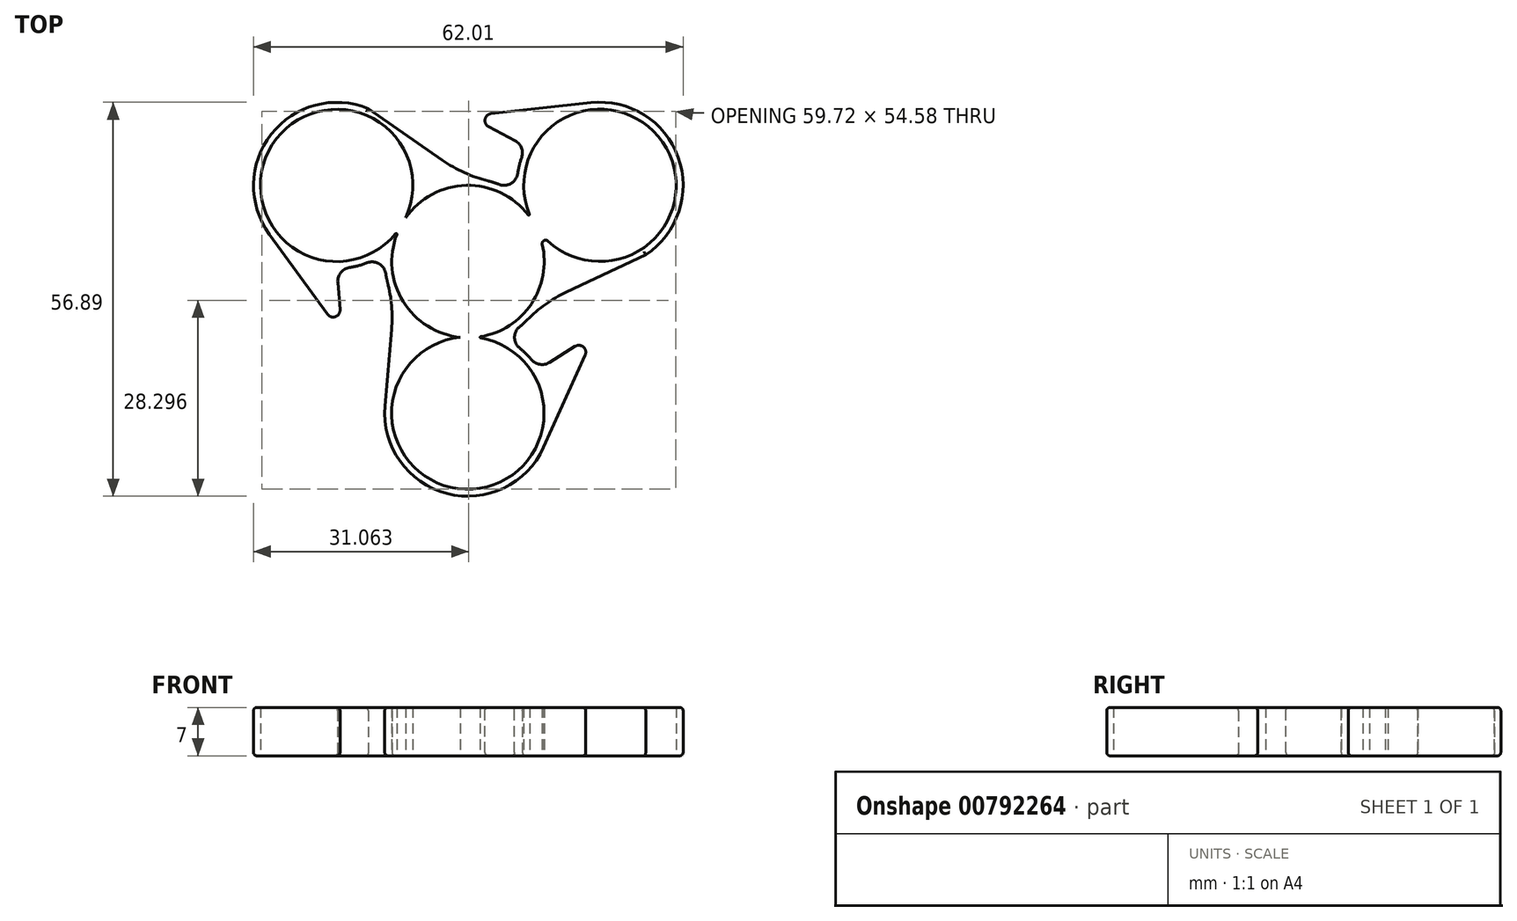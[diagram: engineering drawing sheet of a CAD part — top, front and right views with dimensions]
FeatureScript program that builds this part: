
annotation { "Feature Type Name" : "Feature", "Feature Type Description" : "" }
export const myFeature = defineFeature(function(context is Context, id is Id, definition is map)
    precondition{}
    {
        {
            var Q0;
            Q0=qCreatedBy(makeId("Top.planeOp"),FACE);
            var sketch = newSketch(context, id + "F0", { "sketchPlane" : qUnion([Q0])});
            skCircle(sketch, "E0", {"center": v(-71.75, -0.01) * mm, "radius": 11 * mm});
            skPoint(sketch, "E0.centerSnap0", {"position": v(-71.75, 10.99) * mm});
            skCircle(sketch, "E1", {"center": v(-71.73, 21.88) * mm, "radius": 11 * mm});
            skPoint(sketch, "E2.0.midPoint", {"position": v(-81.26, 16.38) * mm});
            skCircle(sketch, "E3", {"center": v(-52.68, 32.88) * mm, "radius": 11 * mm});
            skPoint(sketch, "E3.centerSnap0", {"position": v(-62.2, 27.38) * mm});
            skLineSegment(sketch, "E4.0", {"start": v(-52.68, 32.88) * mm, "end": v(-62.2, 27.38) * mm, "construction": true});
            skLineSegment(sketch, "E5.0", {"start": v(-71.73, 21.88) * mm, "end": v(-81.26, 16.38) * mm, "construction": true});
            skCircle(sketch, "E6", {"center": v(-90.7, 32.86) * mm, "radius": 11 * mm});
            skPoint(sketch, "E6.centerSnap0", {"position": v(-81.17, 27.36) * mm});
            skLineSegment(sketch, "E7.0", {"start": v(-90.7, 32.86) * mm, "end": v(-81.17, 27.36) * mm, "construction": true});
            skLineSegment(sketch, "E8.0", {"start": v(-71.64, 21.86) * mm, "end": v(-62.11, 16.36) * mm, "construction": true});
            skCircle(sketch, "E9.0", {"center": v(-71.75, -0.01) * mm, "radius": 12 * mm});
            skCircle(sketch, "E10.0", {"center": v(-52.68, 32.88) * mm, "radius": 12 * mm});
            skCircle(sketch, "E11.0", {"center": v(-90.7, 32.86) * mm, "radius": 12 * mm});
            skCircle(sketch, "E12.0", {"center": v(-71.73, 21.88) * mm, "radius": 12 * mm});
            skLineSegment(sketch, "E13", {"start": v(-71.64, 33.88) * mm, "end": v(-86.14, 43.97) * mm});
            skLineSegment(sketch, "E14", {"start": v(-82.4, 16.38) * mm, "end": v(-83.8, 0) * mm});
            skLineSegment(sketch, "E15", {"start": v(-61.52, 15.57) * mm, "end": v(-46.07, 22.86) * mm});
            skLineSegment(sketch, "E16", {"start": v(-89.92, 11.38) * mm, "end": v(-100.4, 25.81) * mm});
            skLineSegment(sketch, "E17", {"start": v(-53.45, 11.36) * mm, "end": v(-60.82, -4.95) * mm});
            skPoint(sketch, "E18", {"position": v(-71.64, 32.88) * mm});
            skLineSegment(sketch, "E19", {"start": v(-71.64, 42.88) * mm, "end": v(-53.98, 44.8) * mm});
            skLineSegment(sketch, "E20", {"start": v(-89.92, 11.38) * mm, "end": v(-90.7, 20.86) * mm});
            skPoint(sketch, "E21", {"position": v(-63.3, 38.48) * mm});
            skLineSegment(sketch, "E22", {"start": v(-71.64, 42.88) * mm, "end": v(-63.3, 38.48) * mm});
            skPoint(sketch, "E23", {"position": v(-61.56, 6.32) * mm});
            skLineSegment(sketch, "E24", {"start": v(-53.45, 11.36) * mm, "end": v(-61.56, 6.32) * mm});
            skSolve(sketch);
        }
        {
            var Q0;
            {var subQ0=sQuery(id+"F0.wireOp",EDGE,"E12.0");var subQ1=sQuery(id+"F0.wireOp",EDGE,"E6");var subQ9=makeQuery(id+"F0.imprint","INTERSECT",VERTEX,{"disambiguationData":[OD(0.0)],"derivedFrom":[subQ1,subQ0]});Q0=makeQuery(id+"F0.imprint","IMPRINT",FACE,{"disambiguationData":[TD([[makeQuery(id+"F0.imprint","IMPRINT",EDGE,{"disambiguationData":[TD([[subQ9,1.0]])],"derivedFrom":subQ1}),-1.0]])]});}
            var Q1;
            {var subQ0=sQuery(id+"F0.wireOp",EDGE,"E12.0");var subQ1=sQuery(id+"F0.wireOp",EDGE,"E3");var subQ9=makeQuery(id+"F0.imprint","INTERSECT",VERTEX,{"disambiguationData":[OD(0.0)],"derivedFrom":[subQ1,subQ0]});Q1=makeQuery(id+"F0.imprint","IMPRINT",FACE,{"disambiguationData":[TD([[makeQuery(id+"F0.imprint","IMPRINT",EDGE,{"disambiguationData":[TD([[subQ9,1.0]])],"derivedFrom":subQ1}),-1.0]])]});}
            var Q2;
            {var subQ0=sQuery(id+"F0.wireOp",EDGE,"E13");var subQ1=sQuery(id+"F0.wireOp",EDGE,"E11.0");var subQ2=makeQuery(id+"F0.imprint","INTERSECT",VERTEX,{"disambiguationData":[OD(1.0)],"derivedFrom":[subQ1,subQ0]});Q2=makeQuery(id+"F0.imprint","IMPRINT",FACE,{"disambiguationData":[TD([[makeQuery(id+"F0.imprint","IMPRINT",EDGE,{"disambiguationData":[TD([[subQ2,1.0]])],"derivedFrom":subQ1}),-1.0]])]});}
            var Q3;
            {var subQ0=sQuery(id+"F0.wireOp",EDGE,"E15");var subQ1=sQuery(id+"F0.wireOp",EDGE,"E10.0");var subQ2=makeQuery(id+"F0.imprint","INTERSECT",VERTEX,{"disambiguationData":[OD(1.0)],"derivedFrom":[subQ1,subQ0]});Q3=makeQuery(id+"F0.imprint","IMPRINT",FACE,{"disambiguationData":[TD([[makeQuery(id+"F0.imprint","IMPRINT",EDGE,{"disambiguationData":[TD([[subQ2,1.0]])],"derivedFrom":subQ1}),-1.0]])]});}
            var Q4;
            {var subQ0=sQuery(id+"F0.wireOp",EDGE,"E14");var subQ1=sQuery(id+"F0.wireOp",EDGE,"E9.0");var subQ2=makeQuery(id+"F0.imprint","INTERSECT",VERTEX,{"derivedFrom":[subQ1,subQ0]});Q4=makeQuery(id+"F0.imprint","IMPRINT",FACE,{"disambiguationData":[TD([[makeQuery(id+"F0.imprint","IMPRINT",EDGE,{"disambiguationData":[TD([[subQ2,1.0]])],"derivedFrom":subQ1}),-1.0]])]});}
            var Q5;
            {var subQ0=sQuery(id+"F0.wireOp",EDGE,"E12.0");var subQ1=sQuery(id+"F0.wireOp",EDGE,"E0");var subQ7=makeQuery(id+"F0.imprint","INTERSECT",VERTEX,{"disambiguationData":[OD(0.0)],"derivedFrom":[subQ1,subQ0]});Q5=makeQuery(id+"F0.imprint","IMPRINT",FACE,{"disambiguationData":[TD([[makeQuery(id+"F0.imprint","IMPRINT",EDGE,{"disambiguationData":[TD([[subQ7,1.0]])],"derivedFrom":subQ1}),-1.0]])]});}
            var Q6;
            {var subQ1=sQuery(id+"F0.wireOp",EDGE,"E1");var subQ6=sQuery(id+"F0.wireOp",EDGE,"E9.0");var subQ8=makeQuery(id+"F0.imprint","INTERSECT",VERTEX,{"disambiguationData":[OD(1.0)],"derivedFrom":[subQ1,subQ6]});Q6=makeQuery(id+"F0.imprint","IMPRINT",FACE,{"disambiguationData":[TD([[makeQuery(id+"F0.imprint","IMPRINT",EDGE,{"disambiguationData":[TD([[subQ8,-1.0]])],"derivedFrom":subQ1}),-1.0]])]});}
            var Q7;
            {var subQ1=sQuery(id+"F0.wireOp",EDGE,"E11.0");var subQ3=sQuery(id+"F0.wireOp",EDGE,"E1");var subQ4=makeQuery(id+"F0.imprint","INTERSECT",VERTEX,{"disambiguationData":[OD(1.0)],"derivedFrom":[subQ3,subQ1]});Q7=makeQuery(id+"F0.imprint","IMPRINT",FACE,{"disambiguationData":[TD([[makeQuery(id+"F0.imprint","IMPRINT",EDGE,{"disambiguationData":[TD([[subQ4,-1.0]])],"derivedFrom":subQ3}),-1.0]])]});}
            var Q8;
            {var subQ0=sQuery(id+"F0.wireOp",EDGE,"E11.0");var subQ1=sQuery(id+"F0.wireOp",EDGE,"E1");var subQ2=makeQuery(id+"F0.imprint","INTERSECT",VERTEX,{"disambiguationData":[OD(0.0)],"derivedFrom":[subQ1,subQ0]});Q8=makeQuery(id+"F0.imprint","IMPRINT",FACE,{"disambiguationData":[TD([[makeQuery(id+"F0.imprint","IMPRINT",EDGE,{"disambiguationData":[TD([[subQ2,1.0]])],"derivedFrom":subQ1}),-1.0]])]});}
            var Q9;
            {var subQ0=sQuery(id+"F0.wireOp",EDGE,"E3");var subQ1=sQuery(id+"F0.wireOp",EDGE,"E1");var subQ2=makeQuery(id+"F0.imprint","INTERSECT",VERTEX,{"derivedFrom":[subQ1,subQ0]});Q9=makeQuery(id+"F0.imprint","IMPRINT",FACE,{"disambiguationData":[TD([[makeQuery(id+"F0.imprint","IMPRINT",EDGE,{"disambiguationData":[TD([[subQ2,-1.0]])],"derivedFrom":subQ1}),-1.0]])]});}
            var Q10;
            {var subQ0=sQuery(id+"F0.wireOp",EDGE,"E6");var subQ1=sQuery(id+"F0.wireOp",EDGE,"E1");var subQ2=makeQuery(id+"F0.imprint","INTERSECT",VERTEX,{"disambiguationData":[OD(1.0)],"derivedFrom":[subQ1,subQ0]});Q10=makeQuery(id+"F0.imprint","IMPRINT",FACE,{"disambiguationData":[TD([[makeQuery(id+"F0.imprint","IMPRINT",EDGE,{"disambiguationData":[TD([[subQ2,-1.0]])],"derivedFrom":subQ1}),-1.0]])]});}
            var Q11;
            {var subQ0=sQuery(id+"F0.wireOp",EDGE,"E1");var subQ1=sQuery(id+"F0.wireOp",EDGE,"E0");var subQ2=makeQuery(id+"F0.imprint","INTERSECT",VERTEX,{"disambiguationData":[OD(0.0)],"derivedFrom":[subQ1,subQ0]});Q11=makeQuery(id+"F0.imprint","IMPRINT",FACE,{"disambiguationData":[TD([[makeQuery(id+"F0.imprint","IMPRINT",EDGE,{"disambiguationData":[TD([[subQ2,1.0]])],"derivedFrom":subQ1}),-1.0]])]});}
            var Q12;
            {var subQ0=sQuery(id+"F0.wireOp",EDGE,"E16");Q12=makeQuery(id+"F0.imprint","IMPRINT",FACE,{"disambiguationData":[TD([[makeQuery(id+"F0.imprint","IMPRINT",EDGE,{"derivedFrom":subQ0}),-1.0]])]});}
            var Q13;
            {var subQ0=sQuery(id+"F0.wireOp",EDGE,"E17");Q13=makeQuery(id+"F0.imprint","IMPRINT",FACE,{"disambiguationData":[TD([[makeQuery(id+"F0.imprint","IMPRINT",EDGE,{"derivedFrom":subQ0}),-1.0]])]});}
            var Q14;
            {var subQ0=sQuery(id+"F0.wireOp",EDGE,"E19");Q14=makeQuery(id+"F0.imprint","IMPRINT",FACE,{"disambiguationData":[TD([[makeQuery(id+"F0.imprint","IMPRINT",EDGE,{"derivedFrom":subQ0}),-1.0]])]});}
            extrude(context, id + "F1", {"entities" : qUnion([Q0, Q1, Q2, Q3, Q4, Q5, Q6, Q7, Q8, Q9, Q10, Q11, Q12, Q13, Q14]), "depth" : 7 * mm, "offsetDistance" : 25 * mm});
        }
        {
            var Q0;
            {var subQ0=sQuery(id+"F0.wireOp",EDGE,"E12.0");var subQ1=sQuery(id+"F0.wireOp",EDGE,"E9.0");Q0=makeQuery(id+"F1.opExtrude","SWEPT_EDGE",EDGE,{"disambiguationData":[OSD([subQ1,subQ0]),TDD([makeQuery(id+"F0.imprint","INTERSECT",VERTEX,{"disambiguationData":[OD(0.0)],"derivedFrom":[subQ1,subQ0]})])]});}
            var Q1;
            {var subQ0=sQuery(id+"F0.wireOp",EDGE,"E12.0");var subQ1=sQuery(id+"F0.wireOp",EDGE,"E10.0");Q1=makeQuery(id+"F1.opExtrude","SWEPT_EDGE",EDGE,{"disambiguationData":[OSD([subQ1,subQ0]),TDD([makeQuery(id+"F0.imprint","INTERSECT",VERTEX,{"disambiguationData":[OD(0.0)],"derivedFrom":[subQ1,subQ0]})])]});}
            var Q2;
            {var subQ0=sQuery(id+"F0.wireOp",EDGE,"E12.0");var subQ1=sQuery(id+"F0.wireOp",EDGE,"E11.0");Q2=makeQuery(id+"F1.opExtrude","SWEPT_EDGE",EDGE,{"disambiguationData":[OSD([subQ1,subQ0]),TDD([makeQuery(id+"F0.imprint","INTERSECT",VERTEX,{"disambiguationData":[OD(0.0)],"derivedFrom":[subQ1,subQ0]})])]});}
            fillet(context, id + "F2", {"entities" : qUnion([Q0, Q1, Q2]), "radius" : 2 * mm, "tangentPropagation" : true, "allowEdgeOverflow" : false});
        }
        {
            var Q0;
            Q0=makeQuery(id+"F1.opExtrude","SWEPT_EDGE",EDGE,{"disambiguationData":[OSD([sQuery(id+"F0.wireOp",EDGE,"E1"),sQuery(id+"F0.wireOp",EDGE,"E3")])]});
            var Q1;
            Q1=makeQuery(id+"F1.opExtrude","SWEPT_EDGE",EDGE,{"disambiguationData":[OSD([sQuery(id+"F0.wireOp",EDGE,"E1"),sQuery(id+"F0.wireOp",EDGE,"E6")])]});
            var Q2;
            Q2=makeQuery(id+"F1.opExtrude","SWEPT_EDGE",EDGE,{"disambiguationData":[OSD([sQuery(id+"F0.wireOp",EDGE,"E0"),sQuery(id+"F0.wireOp",EDGE,"E1")])]});
            fillet(context, id + "F3", {"entities" : qUnion([Q0, Q1, Q2]), "radius" : .1 * mm, "tangentPropagation" : true, "allowEdgeOverflow" : false});
        }
        {
            var Q0;
            {var subQ0=sQuery(id+"F0.wireOp",EDGE,"E6");var subQ1=sQuery(id+"F0.wireOp",EDGE,"E1");var subQ2=makeQuery(id+"F0.imprint","INTERSECT",VERTEX,{"disambiguationData":[OD(0.0)],"derivedFrom":[subQ1,subQ0]});Q0=makeQuery(id+"F0.imprint","IMPRINT",FACE,{"disambiguationData":[TD([[makeQuery(id+"F0.imprint","IMPRINT",EDGE,{"disambiguationData":[TD([[subQ2,1.0]])],"derivedFrom":subQ1}),-1.0]])]});}
            var Q1;
            {var subQ0=sQuery(id+"F0.wireOp",EDGE,"E10.0");var subQ1=sQuery(id+"F0.wireOp",EDGE,"E1");var subQ2=makeQuery(id+"F0.imprint","INTERSECT",VERTEX,{"disambiguationData":[OD(0.0)],"derivedFrom":[subQ1,subQ0]});Q1=makeQuery(id+"F0.imprint","IMPRINT",FACE,{"disambiguationData":[TD([[makeQuery(id+"F0.imprint","IMPRINT",EDGE,{"disambiguationData":[TD([[subQ2,-1.0]])],"derivedFrom":subQ1}),-1.0]])]});}
            var Q2;
            {var subQ0=sQuery(id+"F0.wireOp",EDGE,"E1");var subQ1=sQuery(id+"F0.wireOp",EDGE,"E0");var subQ2=makeQuery(id+"F0.imprint","INTERSECT",VERTEX,{"disambiguationData":[OD(1.0)],"derivedFrom":[subQ1,subQ0]});Q2=makeQuery(id+"F0.imprint","IMPRINT",FACE,{"disambiguationData":[TD([[makeQuery(id+"F0.imprint","IMPRINT",EDGE,{"disambiguationData":[TD([[subQ2,-1.0]])],"derivedFrom":subQ1}),-1.0]])]});}
            extrude(context, id + "F4", {"entities" : qUnion([Q0, Q1, Q2]), "operationType" : NewBodyOperationType.ADD, "depth" : 7 * mm, "offsetDistance" : 25 * mm});
        }
        {
            var Q0;
            Q0=makeQuery(id+"F4.opExtrude","SWEPT_EDGE",EDGE,{"disambiguationData":[OSD([sQuery(id+"F0.wireOp",EDGE,"E1"),sQuery(id+"F0.wireOp",EDGE,"E3")])]});
            var Q1;
            {var subQ0=sQuery(id+"F0.wireOp",EDGE,"E1");var subQ2=sQuery(id+"F0.wireOp",EDGE,"E3");Q1=makeQuery(id+"F3.opFillet","BLEND_EDGE",EDGE,{"blendedFrom":[makeQuery(id+"F1.opExtrude","SWEPT_EDGE",EDGE,{"disambiguationData":[OSD([subQ0,subQ2])]}),makeQuery(id+"F1.opExtrude","SWEPT_FACE",FACE,{"disambiguationData":[OSD([subQ0]),TDD([makeQuery(id+"F0.imprint","IMPRINT",EDGE,{"disambiguationData":[TD([[makeQuery(id+"F0.imprint","INTERSECT",VERTEX,{"derivedFrom":[subQ0,subQ2]}),-1.0]])],"derivedFrom":subQ0}),makeQuery(id+"F0.imprint","IMPRINT",EDGE,{"disambiguationData":[TD([[makeQuery(id+"F0.imprint","INTERSECT",VERTEX,{"disambiguationData":[OD(0.0)],"derivedFrom":[subQ0,sQuery(id+"F0.wireOp",EDGE,"E11.0")]}),1.0]])],"derivedFrom":subQ0})])]})],"blendedInto":[makeQuery(id+"F1.opExtrude","SWEPT_FACE",FACE,{"disambiguationData":[OSD([subQ0]),TDD([makeQuery(id+"F0.imprint","IMPRINT",EDGE,{"disambiguationData":[TD([[makeQuery(id+"F0.imprint","INTERSECT",VERTEX,{"derivedFrom":[subQ0,subQ2]}),-1.0]])],"derivedFrom":subQ0}),makeQuery(id+"F0.imprint","IMPRINT",EDGE,{"disambiguationData":[TD([[makeQuery(id+"F0.imprint","INTERSECT",VERTEX,{"disambiguationData":[OD(0.0)],"derivedFrom":[subQ0,sQuery(id+"F0.wireOp",EDGE,"E11.0")]}),1.0]])],"derivedFrom":subQ0})])]})]});}
            fillet(context, id + "F5", {"entities" : qUnion([Q0, Q1]), "radius" : .5 * mm, "tangentPropagation" : true, "allowEdgeOverflow" : false});
        }
        {
            var Q0;
            Q0=makeQuery(id+"F1.opExtrude","SWEPT_EDGE",EDGE,{"disambiguationData":[OSD([sQuery(id+"F0.wireOp",EDGE,"E11.0"),sQuery(id+"F0.wireOp",EDGE,"E20")])]});
            var Q1;
            Q1=makeQuery(id+"F1.opExtrude","SWEPT_EDGE",EDGE,{"disambiguationData":[OSD([sQuery(id+"F0.wireOp",EDGE,"E10.0"),sQuery(id+"F0.wireOp",EDGE,"E22")])]});
            var Q2;
            Q2=makeQuery(id+"F1.opExtrude","SWEPT_EDGE",EDGE,{"disambiguationData":[OSD([sQuery(id+"F0.wireOp",EDGE,"E9.0"),sQuery(id+"F0.wireOp",EDGE,"E24")])]});
            fillet(context, id + "F6", {"entities" : qUnion([Q0, Q1, Q2]), "radius" : 2 * mm, "tangentPropagation" : true, "allowEdgeOverflow" : false});
        }
        {
            var Q0;
            Q0=makeQuery(id+"F1.opExtrude","SWEPT_EDGE",EDGE,{"disambiguationData":[OSD([sQuery(id+"F0.wireOp",EDGE,"E17"),sQuery(id+"F0.wireOp",EDGE,"E24")])]});
            var Q1;
            Q1=makeQuery(id+"F1.opExtrude","SWEPT_EDGE",EDGE,{"disambiguationData":[OSD([sQuery(id+"F0.wireOp",EDGE,"E19"),sQuery(id+"F0.wireOp",EDGE,"E22")])]});
            var Q2;
            Q2=makeQuery(id+"F1.opExtrude","SWEPT_EDGE",EDGE,{"disambiguationData":[OSD([sQuery(id+"F0.wireOp",EDGE,"E16"),sQuery(id+"F0.wireOp",EDGE,"E20")])]});
            fillet(context, id + "F7", {"entities" : qUnion([Q0, Q1, Q2]), "radius" : 1 * mm, "tangentPropagation" : true, "allowEdgeOverflow" : false});
        }
        {
            var Q0;
            Q0=makeQuery(id+"F1.opExtrude","SWEPT_EDGE",EDGE,{"disambiguationData":[OSD([sQuery(id+"F0.wireOp",EDGE,"E12.0"),sQuery(id+"F0.wireOp",EDGE,"E14")])]});
            var Q1;
            Q1=makeQuery(id+"F1.opExtrude","SWEPT_EDGE",EDGE,{"disambiguationData":[OSD([sQuery(id+"F0.wireOp",EDGE,"E12.0"),sQuery(id+"F0.wireOp",EDGE,"E15")])]});
            var Q2;
            Q2=makeQuery(id+"F1.opExtrude","SWEPT_EDGE",EDGE,{"disambiguationData":[OSD([sQuery(id+"F0.wireOp",EDGE,"E12.0"),sQuery(id+"F0.wireOp",EDGE,"E13")])]});
            fillet(context, id + "F8", {"entities" : qUnion([Q0, Q1, Q2]), "radius" : 20 * mm, "tangentPropagation" : true, "allowEdgeOverflow" : false});
        }
        {
            var Q0;
            {var subQ0=sQuery(id+"F0.wireOp",EDGE,"E9.0");Q0=makeQuery(id+"F1.opExtrude","CAP_EDGE",EDGE,{"disambiguationData":[OSD([subQ0]),TDD([makeQuery(id+"F0.imprint","IMPRINT",EDGE,{"disambiguationData":[TD([[makeQuery(id+"F0.imprint","INTERSECT",VERTEX,{"derivedFrom":[subQ0,sQuery(id+"F0.wireOp",EDGE,"E17")]}),1.0]])],"derivedFrom":subQ0})])],"isStart":false});}
            var Q1;
            Q1=makeQuery(id+"F1.opExtrude","CAP_EDGE",EDGE,{"disambiguationData":[OSD([sQuery(id+"F0.wireOp",EDGE,"E17")])],"isStart":false});
            var Q2;
            {var subQ0=sQuery(id+"F0.wireOp",EDGE,"E12.0");var subQ1=sQuery(id+"F0.wireOp",EDGE,"E10.0");var subQ2=sQuery(id+"F0.wireOp",EDGE,"E3");var subQ3=sQuery(id+"F0.wireOp",EDGE,"E1");var subQ4=sQuery(id+"F0.wireOp",EDGE,"E11.0");var subQ5=sQuery(id+"F0.wireOp",EDGE,"E6");var subQ6=sQuery(id+"F0.wireOp",EDGE,"E9.0");var subQ7=sQuery(id+"F0.wireOp",EDGE,"E0");var subQ8=sQuery(id+"F0.wireOp",EDGE,"E15");Q2=makeQuery(id+"F8.opFillet","BLEND_EDGE",EDGE,{"blendedFrom":[makeQuery(id+"F1.opExtrude","SWEPT_EDGE",EDGE,{"disambiguationData":[OSD([subQ0,subQ8])]}),makeQuery(id+"F4.boolean.opBoolean","MERGE",FACE,{"derivedFrom":[makeQuery(id+"F1.opExtrude","CAP_FACE",FACE,{"disambiguationData":[OSD([subQ7,subQ3,subQ2,subQ5,subQ6,subQ1,subQ4,subQ0,sQuery(id+"F0.wireOp",EDGE,"E13"),sQuery(id+"F0.wireOp",EDGE,"E14"),subQ8,sQuery(id+"F0.wireOp",EDGE,"E16"),sQuery(id+"F0.wireOp",EDGE,"E17"),sQuery(id+"F0.wireOp",EDGE,"E19"),sQuery(id+"F0.wireOp",EDGE,"E20"),sQuery(id+"F0.wireOp",EDGE,"E22"),sQuery(id+"F0.wireOp",EDGE,"E24")])],"isStart":false}),makeQuery(id+"F4.opExtrude","CAP_FACE",FACE,{"disambiguationData":[OSD([subQ7,subQ3,subQ6,subQ0])],"isStart":false}),makeQuery(id+"F4.opExtrude","CAP_FACE",FACE,{"disambiguationData":[OSD([subQ3,subQ5,subQ4,subQ0])],"isStart":false}),makeQuery(id+"F4.opExtrude","CAP_FACE",FACE,{"disambiguationData":[OSD([subQ3,subQ2,subQ1,subQ0])],"isStart":false})]})],"blendedInto":[makeQuery(id+"F4.boolean.opBoolean","MERGE",FACE,{"derivedFrom":[makeQuery(id+"F1.opExtrude","CAP_FACE",FACE,{"disambiguationData":[OSD([subQ7,subQ3,subQ2,subQ5,subQ6,subQ1,subQ4,subQ0,sQuery(id+"F0.wireOp",EDGE,"E13"),sQuery(id+"F0.wireOp",EDGE,"E14"),subQ8,sQuery(id+"F0.wireOp",EDGE,"E16"),sQuery(id+"F0.wireOp",EDGE,"E17"),sQuery(id+"F0.wireOp",EDGE,"E19"),sQuery(id+"F0.wireOp",EDGE,"E20"),sQuery(id+"F0.wireOp",EDGE,"E22"),sQuery(id+"F0.wireOp",EDGE,"E24")])],"isStart":false}),makeQuery(id+"F4.opExtrude","CAP_FACE",FACE,{"disambiguationData":[OSD([subQ7,subQ3,subQ6,subQ0])],"isStart":false}),makeQuery(id+"F4.opExtrude","CAP_FACE",FACE,{"disambiguationData":[OSD([subQ3,subQ5,subQ4,subQ0])],"isStart":false}),makeQuery(id+"F4.opExtrude","CAP_FACE",FACE,{"disambiguationData":[OSD([subQ3,subQ2,subQ1,subQ0])],"isStart":false})]})]});}
            var Q3;
            {var subQ0=sQuery(id+"F0.wireOp",EDGE,"E12.0");Q3=makeQuery(id+"F1.opExtrude","CAP_EDGE",EDGE,{"disambiguationData":[OSD([subQ0]),TDD([makeQuery(id+"F0.imprint","IMPRINT",EDGE,{"disambiguationData":[TD([[makeQuery(id+"F0.imprint","INTERSECT",VERTEX,{"derivedFrom":[subQ0,sQuery(id+"F0.wireOp",EDGE,"E15")]}),1.0]])],"derivedFrom":subQ0})])],"isStart":false});}
            var Q4;
            {var subQ0=sQuery(id+"F0.wireOp",EDGE,"E12.0");var subQ1=sQuery(id+"F0.wireOp",EDGE,"E9.0");Q4=makeQuery(id+"F2.opFillet","BLEND_EDGE",EDGE,{"blendedFrom":[makeQuery(id+"F1.opExtrude","SWEPT_EDGE",EDGE,{"disambiguationData":[OSD([subQ1,subQ0]),TDD([makeQuery(id+"F0.imprint","INTERSECT",VERTEX,{"disambiguationData":[OD(0.0)],"derivedFrom":[subQ1,subQ0]})])]}),makeQuery(id+"F1.opExtrude","CAP_FACE",FACE,{"disambiguationData":[OSD([sQuery(id+"F0.wireOp",EDGE,"E0"),sQuery(id+"F0.wireOp",EDGE,"E1"),sQuery(id+"F0.wireOp",EDGE,"E3"),sQuery(id+"F0.wireOp",EDGE,"E6"),subQ1,sQuery(id+"F0.wireOp",EDGE,"E10.0"),sQuery(id+"F0.wireOp",EDGE,"E11.0"),subQ0,sQuery(id+"F0.wireOp",EDGE,"E13"),sQuery(id+"F0.wireOp",EDGE,"E14"),sQuery(id+"F0.wireOp",EDGE,"E15"),sQuery(id+"F0.wireOp",EDGE,"E16"),sQuery(id+"F0.wireOp",EDGE,"E17"),sQuery(id+"F0.wireOp",EDGE,"E19"),sQuery(id+"F0.wireOp",EDGE,"E20"),sQuery(id+"F0.wireOp",EDGE,"E22"),sQuery(id+"F0.wireOp",EDGE,"E24")])],"isStart":false})],"blendedInto":[makeQuery(id+"F1.opExtrude","CAP_FACE",FACE,{"disambiguationData":[OSD([sQuery(id+"F0.wireOp",EDGE,"E0"),sQuery(id+"F0.wireOp",EDGE,"E1"),sQuery(id+"F0.wireOp",EDGE,"E3"),sQuery(id+"F0.wireOp",EDGE,"E6"),subQ1,sQuery(id+"F0.wireOp",EDGE,"E10.0"),sQuery(id+"F0.wireOp",EDGE,"E11.0"),subQ0,sQuery(id+"F0.wireOp",EDGE,"E13"),sQuery(id+"F0.wireOp",EDGE,"E14"),sQuery(id+"F0.wireOp",EDGE,"E15"),sQuery(id+"F0.wireOp",EDGE,"E16"),sQuery(id+"F0.wireOp",EDGE,"E17"),sQuery(id+"F0.wireOp",EDGE,"E19"),sQuery(id+"F0.wireOp",EDGE,"E20"),sQuery(id+"F0.wireOp",EDGE,"E22"),sQuery(id+"F0.wireOp",EDGE,"E24")])],"isStart":false})]});}
            var Q5;
            {var subQ0=sQuery(id+"F0.wireOp",EDGE,"E9.0");Q5=makeQuery(id+"F1.opExtrude","CAP_EDGE",EDGE,{"disambiguationData":[OSD([subQ0]),TDD([makeQuery(id+"F0.imprint","IMPRINT",EDGE,{"disambiguationData":[TD([[makeQuery(id+"F0.imprint","INTERSECT",VERTEX,{"derivedFrom":[subQ0,sQuery(id+"F0.wireOp",EDGE,"E24")]}),-1.0]])],"derivedFrom":subQ0})])],"isStart":false});}
            var Q6;
            Q6=makeQuery(id+"F1.opExtrude","CAP_EDGE",EDGE,{"disambiguationData":[OSD([sQuery(id+"F0.wireOp",EDGE,"E24")])],"isStart":false});
            var Q7;
            {var subQ0=sQuery(id+"F0.wireOp",EDGE,"E12.0");var subQ1=sQuery(id+"F0.wireOp",EDGE,"E10.0");var subQ2=sQuery(id+"F0.wireOp",EDGE,"E3");var subQ3=sQuery(id+"F0.wireOp",EDGE,"E1");var subQ4=sQuery(id+"F0.wireOp",EDGE,"E11.0");var subQ5=sQuery(id+"F0.wireOp",EDGE,"E6");var subQ6=sQuery(id+"F0.wireOp",EDGE,"E9.0");var subQ7=sQuery(id+"F0.wireOp",EDGE,"E0");var subQ8=sQuery(id+"F0.wireOp",EDGE,"E24");Q7=makeQuery(id+"F6.opFillet","BLEND_EDGE",EDGE,{"blendedFrom":[makeQuery(id+"F1.opExtrude","SWEPT_EDGE",EDGE,{"disambiguationData":[OSD([subQ6,subQ8])]}),makeQuery(id+"F4.boolean.opBoolean","MERGE",FACE,{"derivedFrom":[makeQuery(id+"F1.opExtrude","CAP_FACE",FACE,{"disambiguationData":[OSD([subQ7,subQ3,subQ2,subQ5,subQ6,subQ1,subQ4,subQ0,sQuery(id+"F0.wireOp",EDGE,"E13"),sQuery(id+"F0.wireOp",EDGE,"E14"),sQuery(id+"F0.wireOp",EDGE,"E15"),sQuery(id+"F0.wireOp",EDGE,"E16"),sQuery(id+"F0.wireOp",EDGE,"E17"),sQuery(id+"F0.wireOp",EDGE,"E19"),sQuery(id+"F0.wireOp",EDGE,"E20"),sQuery(id+"F0.wireOp",EDGE,"E22"),subQ8])],"isStart":false}),makeQuery(id+"F4.opExtrude","CAP_FACE",FACE,{"disambiguationData":[OSD([subQ7,subQ3,subQ6,subQ0])],"isStart":false}),makeQuery(id+"F4.opExtrude","CAP_FACE",FACE,{"disambiguationData":[OSD([subQ3,subQ5,subQ4,subQ0])],"isStart":false}),makeQuery(id+"F4.opExtrude","CAP_FACE",FACE,{"disambiguationData":[OSD([subQ3,subQ2,subQ1,subQ0])],"isStart":false})]})],"blendedInto":[makeQuery(id+"F4.boolean.opBoolean","MERGE",FACE,{"derivedFrom":[makeQuery(id+"F1.opExtrude","CAP_FACE",FACE,{"disambiguationData":[OSD([subQ7,subQ3,subQ2,subQ5,subQ6,subQ1,subQ4,subQ0,sQuery(id+"F0.wireOp",EDGE,"E13"),sQuery(id+"F0.wireOp",EDGE,"E14"),sQuery(id+"F0.wireOp",EDGE,"E15"),sQuery(id+"F0.wireOp",EDGE,"E16"),sQuery(id+"F0.wireOp",EDGE,"E17"),sQuery(id+"F0.wireOp",EDGE,"E19"),sQuery(id+"F0.wireOp",EDGE,"E20"),sQuery(id+"F0.wireOp",EDGE,"E22"),subQ8])],"isStart":false}),makeQuery(id+"F4.opExtrude","CAP_FACE",FACE,{"disambiguationData":[OSD([subQ7,subQ3,subQ6,subQ0])],"isStart":false}),makeQuery(id+"F4.opExtrude","CAP_FACE",FACE,{"disambiguationData":[OSD([subQ3,subQ5,subQ4,subQ0])],"isStart":false}),makeQuery(id+"F4.opExtrude","CAP_FACE",FACE,{"disambiguationData":[OSD([subQ3,subQ2,subQ1,subQ0])],"isStart":false})]})]});}
            var Q8;
            {var subQ0=sQuery(id+"F0.wireOp",EDGE,"E12.0");var subQ1=sQuery(id+"F0.wireOp",EDGE,"E10.0");var subQ2=sQuery(id+"F0.wireOp",EDGE,"E3");var subQ3=sQuery(id+"F0.wireOp",EDGE,"E1");var subQ4=sQuery(id+"F0.wireOp",EDGE,"E11.0");var subQ5=sQuery(id+"F0.wireOp",EDGE,"E6");var subQ6=sQuery(id+"F0.wireOp",EDGE,"E9.0");var subQ7=sQuery(id+"F0.wireOp",EDGE,"E0");var subQ8=sQuery(id+"F0.wireOp",EDGE,"E24");var subQ9=sQuery(id+"F0.wireOp",EDGE,"E17");Q8=makeQuery(id+"F7.opFillet","BLEND_EDGE",EDGE,{"blendedFrom":[makeQuery(id+"F1.opExtrude","SWEPT_EDGE",EDGE,{"disambiguationData":[OSD([subQ9,subQ8])]}),makeQuery(id+"F4.boolean.opBoolean","MERGE",FACE,{"derivedFrom":[makeQuery(id+"F1.opExtrude","CAP_FACE",FACE,{"disambiguationData":[OSD([subQ7,subQ3,subQ2,subQ5,subQ6,subQ1,subQ4,subQ0,sQuery(id+"F0.wireOp",EDGE,"E13"),sQuery(id+"F0.wireOp",EDGE,"E14"),sQuery(id+"F0.wireOp",EDGE,"E15"),sQuery(id+"F0.wireOp",EDGE,"E16"),subQ9,sQuery(id+"F0.wireOp",EDGE,"E19"),sQuery(id+"F0.wireOp",EDGE,"E20"),sQuery(id+"F0.wireOp",EDGE,"E22"),subQ8])],"isStart":false}),makeQuery(id+"F4.opExtrude","CAP_FACE",FACE,{"disambiguationData":[OSD([subQ7,subQ3,subQ6,subQ0])],"isStart":false}),makeQuery(id+"F4.opExtrude","CAP_FACE",FACE,{"disambiguationData":[OSD([subQ3,subQ5,subQ4,subQ0])],"isStart":false}),makeQuery(id+"F4.opExtrude","CAP_FACE",FACE,{"disambiguationData":[OSD([subQ3,subQ2,subQ1,subQ0])],"isStart":false})]})],"blendedInto":[makeQuery(id+"F4.boolean.opBoolean","MERGE",FACE,{"derivedFrom":[makeQuery(id+"F1.opExtrude","CAP_FACE",FACE,{"disambiguationData":[OSD([subQ7,subQ3,subQ2,subQ5,subQ6,subQ1,subQ4,subQ0,sQuery(id+"F0.wireOp",EDGE,"E13"),sQuery(id+"F0.wireOp",EDGE,"E14"),sQuery(id+"F0.wireOp",EDGE,"E15"),sQuery(id+"F0.wireOp",EDGE,"E16"),subQ9,sQuery(id+"F0.wireOp",EDGE,"E19"),sQuery(id+"F0.wireOp",EDGE,"E20"),sQuery(id+"F0.wireOp",EDGE,"E22"),subQ8])],"isStart":false}),makeQuery(id+"F4.opExtrude","CAP_FACE",FACE,{"disambiguationData":[OSD([subQ7,subQ3,subQ6,subQ0])],"isStart":false}),makeQuery(id+"F4.opExtrude","CAP_FACE",FACE,{"disambiguationData":[OSD([subQ3,subQ5,subQ4,subQ0])],"isStart":false}),makeQuery(id+"F4.opExtrude","CAP_FACE",FACE,{"disambiguationData":[OSD([subQ3,subQ2,subQ1,subQ0])],"isStart":false})]})]});}
            var Q9;
            Q9=makeQuery(id+"F1.opExtrude","CAP_EDGE",EDGE,{"disambiguationData":[OSD([sQuery(id+"F0.wireOp",EDGE,"E15")])],"isStart":false});
            var Q10;
            {var subQ0=sQuery(id+"F0.wireOp",EDGE,"E10.0");Q10=makeQuery(id+"F1.opExtrude","CAP_EDGE",EDGE,{"disambiguationData":[OSD([subQ0]),TDD([makeQuery(id+"F0.imprint","IMPRINT",EDGE,{"disambiguationData":[TD([[makeQuery(id+"F0.imprint","INTERSECT",VERTEX,{"disambiguationData":[OD(0.0)],"derivedFrom":[subQ0,sQuery(id+"F0.wireOp",EDGE,"E15")]}),-1.0]])],"derivedFrom":subQ0})])],"isStart":false});}
            fillet(context, id + "F9", {"entities" : qUnion([Q0, Q1, Q2, Q3, Q4, Q5, Q6, Q7, Q8, Q9, Q10]), "radius" : .5 * mm, "tangentPropagation" : true, "allowEdgeOverflow" : false});
        }
        {
            var Q0;
            {var subQ0=sQuery(id+"F0.wireOp",EDGE,"E12.0");var subQ1=sQuery(id+"F0.wireOp",EDGE,"E10.0");var subQ2=sQuery(id+"F0.wireOp",EDGE,"E3");var subQ3=sQuery(id+"F0.wireOp",EDGE,"E1");var subQ4=sQuery(id+"F0.wireOp",EDGE,"E11.0");var subQ5=sQuery(id+"F0.wireOp",EDGE,"E6");var subQ6=sQuery(id+"F0.wireOp",EDGE,"E9.0");var subQ7=sQuery(id+"F0.wireOp",EDGE,"E0");var subQ8=sQuery(id+"F0.wireOp",EDGE,"E14");Q0=makeQuery(id+"F8.opFillet","BLEND_EDGE",EDGE,{"blendedFrom":[makeQuery(id+"F1.opExtrude","SWEPT_EDGE",EDGE,{"disambiguationData":[OSD([subQ0,subQ8])]}),makeQuery(id+"F4.boolean.opBoolean","MERGE",FACE,{"derivedFrom":[makeQuery(id+"F1.opExtrude","CAP_FACE",FACE,{"disambiguationData":[OSD([subQ7,subQ3,subQ2,subQ5,subQ6,subQ1,subQ4,subQ0,sQuery(id+"F0.wireOp",EDGE,"E13"),subQ8,sQuery(id+"F0.wireOp",EDGE,"E15"),sQuery(id+"F0.wireOp",EDGE,"E16"),sQuery(id+"F0.wireOp",EDGE,"E17"),sQuery(id+"F0.wireOp",EDGE,"E19"),sQuery(id+"F0.wireOp",EDGE,"E20"),sQuery(id+"F0.wireOp",EDGE,"E22"),sQuery(id+"F0.wireOp",EDGE,"E24")])],"isStart":true}),makeQuery(id+"F4.opExtrude","CAP_FACE",FACE,{"disambiguationData":[OSD([subQ7,subQ3,subQ6,subQ0])],"isStart":true}),makeQuery(id+"F4.opExtrude","CAP_FACE",FACE,{"disambiguationData":[OSD([subQ3,subQ5,subQ4,subQ0])],"isStart":true}),makeQuery(id+"F4.opExtrude","CAP_FACE",FACE,{"disambiguationData":[OSD([subQ3,subQ2,subQ1,subQ0])],"isStart":true})]})],"blendedInto":[makeQuery(id+"F4.boolean.opBoolean","MERGE",FACE,{"derivedFrom":[makeQuery(id+"F1.opExtrude","CAP_FACE",FACE,{"disambiguationData":[OSD([subQ7,subQ3,subQ2,subQ5,subQ6,subQ1,subQ4,subQ0,sQuery(id+"F0.wireOp",EDGE,"E13"),subQ8,sQuery(id+"F0.wireOp",EDGE,"E15"),sQuery(id+"F0.wireOp",EDGE,"E16"),sQuery(id+"F0.wireOp",EDGE,"E17"),sQuery(id+"F0.wireOp",EDGE,"E19"),sQuery(id+"F0.wireOp",EDGE,"E20"),sQuery(id+"F0.wireOp",EDGE,"E22"),sQuery(id+"F0.wireOp",EDGE,"E24")])],"isStart":true}),makeQuery(id+"F4.opExtrude","CAP_FACE",FACE,{"disambiguationData":[OSD([subQ7,subQ3,subQ6,subQ0])],"isStart":true}),makeQuery(id+"F4.opExtrude","CAP_FACE",FACE,{"disambiguationData":[OSD([subQ3,subQ5,subQ4,subQ0])],"isStart":true}),makeQuery(id+"F4.opExtrude","CAP_FACE",FACE,{"disambiguationData":[OSD([subQ3,subQ2,subQ1,subQ0])],"isStart":true})]})]});}
            var Q1;
            {var subQ0=sQuery(id+"F0.wireOp",EDGE,"E12.0");Q1=makeQuery(id+"F1.opExtrude","CAP_EDGE",EDGE,{"disambiguationData":[OSD([subQ0]),TDD([makeQuery(id+"F0.imprint","IMPRINT",EDGE,{"disambiguationData":[TD([[makeQuery(id+"F0.imprint","INTERSECT",VERTEX,{"derivedFrom":[subQ0,sQuery(id+"F0.wireOp",EDGE,"E14")]}),1.0]])],"derivedFrom":subQ0})])],"isStart":true});}
            var Q2;
            {var subQ0=sQuery(id+"F0.wireOp",EDGE,"E12.0");var subQ1=sQuery(id+"F0.wireOp",EDGE,"E11.0");Q2=makeQuery(id+"F2.opFillet","BLEND_EDGE",EDGE,{"blendedFrom":[makeQuery(id+"F1.opExtrude","SWEPT_EDGE",EDGE,{"disambiguationData":[OSD([subQ1,subQ0]),TDD([makeQuery(id+"F0.imprint","INTERSECT",VERTEX,{"disambiguationData":[OD(0.0)],"derivedFrom":[subQ1,subQ0]})])]}),makeQuery(id+"F1.opExtrude","CAP_FACE",FACE,{"disambiguationData":[OSD([sQuery(id+"F0.wireOp",EDGE,"E0"),sQuery(id+"F0.wireOp",EDGE,"E1"),sQuery(id+"F0.wireOp",EDGE,"E3"),sQuery(id+"F0.wireOp",EDGE,"E6"),sQuery(id+"F0.wireOp",EDGE,"E9.0"),sQuery(id+"F0.wireOp",EDGE,"E10.0"),subQ1,subQ0,sQuery(id+"F0.wireOp",EDGE,"E13"),sQuery(id+"F0.wireOp",EDGE,"E14"),sQuery(id+"F0.wireOp",EDGE,"E15"),sQuery(id+"F0.wireOp",EDGE,"E16"),sQuery(id+"F0.wireOp",EDGE,"E17"),sQuery(id+"F0.wireOp",EDGE,"E19"),sQuery(id+"F0.wireOp",EDGE,"E20"),sQuery(id+"F0.wireOp",EDGE,"E22"),sQuery(id+"F0.wireOp",EDGE,"E24")])],"isStart":true})],"blendedInto":[makeQuery(id+"F1.opExtrude","CAP_FACE",FACE,{"disambiguationData":[OSD([sQuery(id+"F0.wireOp",EDGE,"E0"),sQuery(id+"F0.wireOp",EDGE,"E1"),sQuery(id+"F0.wireOp",EDGE,"E3"),sQuery(id+"F0.wireOp",EDGE,"E6"),sQuery(id+"F0.wireOp",EDGE,"E9.0"),sQuery(id+"F0.wireOp",EDGE,"E10.0"),subQ1,subQ0,sQuery(id+"F0.wireOp",EDGE,"E13"),sQuery(id+"F0.wireOp",EDGE,"E14"),sQuery(id+"F0.wireOp",EDGE,"E15"),sQuery(id+"F0.wireOp",EDGE,"E16"),sQuery(id+"F0.wireOp",EDGE,"E17"),sQuery(id+"F0.wireOp",EDGE,"E19"),sQuery(id+"F0.wireOp",EDGE,"E20"),sQuery(id+"F0.wireOp",EDGE,"E22"),sQuery(id+"F0.wireOp",EDGE,"E24")])],"isStart":true})]});}
            var Q3;
            Q3=makeQuery(id+"F1.opExtrude","CAP_EDGE",EDGE,{"disambiguationData":[OSD([sQuery(id+"F0.wireOp",EDGE,"E14")])],"isStart":true});
            var Q4;
            {var subQ0=sQuery(id+"F0.wireOp",EDGE,"E9.0");Q4=makeQuery(id+"F1.opExtrude","CAP_EDGE",EDGE,{"disambiguationData":[OSD([subQ0]),TDD([makeQuery(id+"F0.imprint","IMPRINT",EDGE,{"disambiguationData":[TD([[makeQuery(id+"F0.imprint","INTERSECT",VERTEX,{"derivedFrom":[subQ0,sQuery(id+"F0.wireOp",EDGE,"E17")]}),1.0]])],"derivedFrom":subQ0})])],"isStart":true});}
            var Q5;
            Q5=makeQuery(id+"F1.opExtrude","CAP_EDGE",EDGE,{"disambiguationData":[OSD([sQuery(id+"F0.wireOp",EDGE,"E17")])],"isStart":true});
            var Q6;
            {var subQ0=sQuery(id+"F0.wireOp",EDGE,"E12.0");var subQ1=sQuery(id+"F0.wireOp",EDGE,"E10.0");var subQ2=sQuery(id+"F0.wireOp",EDGE,"E3");var subQ3=sQuery(id+"F0.wireOp",EDGE,"E1");var subQ4=sQuery(id+"F0.wireOp",EDGE,"E11.0");var subQ5=sQuery(id+"F0.wireOp",EDGE,"E6");var subQ6=sQuery(id+"F0.wireOp",EDGE,"E9.0");var subQ7=sQuery(id+"F0.wireOp",EDGE,"E0");var subQ8=sQuery(id+"F0.wireOp",EDGE,"E24");var subQ9=sQuery(id+"F0.wireOp",EDGE,"E17");Q6=makeQuery(id+"F7.opFillet","BLEND_EDGE",EDGE,{"blendedFrom":[makeQuery(id+"F1.opExtrude","SWEPT_EDGE",EDGE,{"disambiguationData":[OSD([subQ9,subQ8])]}),makeQuery(id+"F4.boolean.opBoolean","MERGE",FACE,{"derivedFrom":[makeQuery(id+"F1.opExtrude","CAP_FACE",FACE,{"disambiguationData":[OSD([subQ7,subQ3,subQ2,subQ5,subQ6,subQ1,subQ4,subQ0,sQuery(id+"F0.wireOp",EDGE,"E13"),sQuery(id+"F0.wireOp",EDGE,"E14"),sQuery(id+"F0.wireOp",EDGE,"E15"),sQuery(id+"F0.wireOp",EDGE,"E16"),subQ9,sQuery(id+"F0.wireOp",EDGE,"E19"),sQuery(id+"F0.wireOp",EDGE,"E20"),sQuery(id+"F0.wireOp",EDGE,"E22"),subQ8])],"isStart":true}),makeQuery(id+"F4.opExtrude","CAP_FACE",FACE,{"disambiguationData":[OSD([subQ7,subQ3,subQ6,subQ0])],"isStart":true}),makeQuery(id+"F4.opExtrude","CAP_FACE",FACE,{"disambiguationData":[OSD([subQ3,subQ5,subQ4,subQ0])],"isStart":true}),makeQuery(id+"F4.opExtrude","CAP_FACE",FACE,{"disambiguationData":[OSD([subQ3,subQ2,subQ1,subQ0])],"isStart":true})]})],"blendedInto":[makeQuery(id+"F4.boolean.opBoolean","MERGE",FACE,{"derivedFrom":[makeQuery(id+"F1.opExtrude","CAP_FACE",FACE,{"disambiguationData":[OSD([subQ7,subQ3,subQ2,subQ5,subQ6,subQ1,subQ4,subQ0,sQuery(id+"F0.wireOp",EDGE,"E13"),sQuery(id+"F0.wireOp",EDGE,"E14"),sQuery(id+"F0.wireOp",EDGE,"E15"),sQuery(id+"F0.wireOp",EDGE,"E16"),subQ9,sQuery(id+"F0.wireOp",EDGE,"E19"),sQuery(id+"F0.wireOp",EDGE,"E20"),sQuery(id+"F0.wireOp",EDGE,"E22"),subQ8])],"isStart":true}),makeQuery(id+"F4.opExtrude","CAP_FACE",FACE,{"disambiguationData":[OSD([subQ7,subQ3,subQ6,subQ0])],"isStart":true}),makeQuery(id+"F4.opExtrude","CAP_FACE",FACE,{"disambiguationData":[OSD([subQ3,subQ5,subQ4,subQ0])],"isStart":true}),makeQuery(id+"F4.opExtrude","CAP_FACE",FACE,{"disambiguationData":[OSD([subQ3,subQ2,subQ1,subQ0])],"isStart":true})]})]});}
            var Q7;
            Q7=makeQuery(id+"F1.opExtrude","CAP_EDGE",EDGE,{"disambiguationData":[OSD([sQuery(id+"F0.wireOp",EDGE,"E24")])],"isStart":true});
            var Q8;
            {var subQ0=sQuery(id+"F0.wireOp",EDGE,"E12.0");var subQ1=sQuery(id+"F0.wireOp",EDGE,"E10.0");var subQ2=sQuery(id+"F0.wireOp",EDGE,"E3");var subQ3=sQuery(id+"F0.wireOp",EDGE,"E1");var subQ4=sQuery(id+"F0.wireOp",EDGE,"E11.0");var subQ5=sQuery(id+"F0.wireOp",EDGE,"E6");var subQ6=sQuery(id+"F0.wireOp",EDGE,"E9.0");var subQ7=sQuery(id+"F0.wireOp",EDGE,"E0");var subQ8=sQuery(id+"F0.wireOp",EDGE,"E24");Q8=makeQuery(id+"F6.opFillet","BLEND_EDGE",EDGE,{"blendedFrom":[makeQuery(id+"F1.opExtrude","SWEPT_EDGE",EDGE,{"disambiguationData":[OSD([subQ6,subQ8])]}),makeQuery(id+"F4.boolean.opBoolean","MERGE",FACE,{"derivedFrom":[makeQuery(id+"F1.opExtrude","CAP_FACE",FACE,{"disambiguationData":[OSD([subQ7,subQ3,subQ2,subQ5,subQ6,subQ1,subQ4,subQ0,sQuery(id+"F0.wireOp",EDGE,"E13"),sQuery(id+"F0.wireOp",EDGE,"E14"),sQuery(id+"F0.wireOp",EDGE,"E15"),sQuery(id+"F0.wireOp",EDGE,"E16"),sQuery(id+"F0.wireOp",EDGE,"E17"),sQuery(id+"F0.wireOp",EDGE,"E19"),sQuery(id+"F0.wireOp",EDGE,"E20"),sQuery(id+"F0.wireOp",EDGE,"E22"),subQ8])],"isStart":true}),makeQuery(id+"F4.opExtrude","CAP_FACE",FACE,{"disambiguationData":[OSD([subQ7,subQ3,subQ6,subQ0])],"isStart":true}),makeQuery(id+"F4.opExtrude","CAP_FACE",FACE,{"disambiguationData":[OSD([subQ3,subQ5,subQ4,subQ0])],"isStart":true}),makeQuery(id+"F4.opExtrude","CAP_FACE",FACE,{"disambiguationData":[OSD([subQ3,subQ2,subQ1,subQ0])],"isStart":true})]})],"blendedInto":[makeQuery(id+"F4.boolean.opBoolean","MERGE",FACE,{"derivedFrom":[makeQuery(id+"F1.opExtrude","CAP_FACE",FACE,{"disambiguationData":[OSD([subQ7,subQ3,subQ2,subQ5,subQ6,subQ1,subQ4,subQ0,sQuery(id+"F0.wireOp",EDGE,"E13"),sQuery(id+"F0.wireOp",EDGE,"E14"),sQuery(id+"F0.wireOp",EDGE,"E15"),sQuery(id+"F0.wireOp",EDGE,"E16"),sQuery(id+"F0.wireOp",EDGE,"E17"),sQuery(id+"F0.wireOp",EDGE,"E19"),sQuery(id+"F0.wireOp",EDGE,"E20"),sQuery(id+"F0.wireOp",EDGE,"E22"),subQ8])],"isStart":true}),makeQuery(id+"F4.opExtrude","CAP_FACE",FACE,{"disambiguationData":[OSD([subQ7,subQ3,subQ6,subQ0])],"isStart":true}),makeQuery(id+"F4.opExtrude","CAP_FACE",FACE,{"disambiguationData":[OSD([subQ3,subQ5,subQ4,subQ0])],"isStart":true}),makeQuery(id+"F4.opExtrude","CAP_FACE",FACE,{"disambiguationData":[OSD([subQ3,subQ2,subQ1,subQ0])],"isStart":true})]})]});}
            var Q9;
            {var subQ0=sQuery(id+"F0.wireOp",EDGE,"E9.0");Q9=makeQuery(id+"F1.opExtrude","CAP_EDGE",EDGE,{"disambiguationData":[OSD([subQ0]),TDD([makeQuery(id+"F0.imprint","IMPRINT",EDGE,{"disambiguationData":[TD([[makeQuery(id+"F0.imprint","INTERSECT",VERTEX,{"derivedFrom":[subQ0,sQuery(id+"F0.wireOp",EDGE,"E24")]}),-1.0]])],"derivedFrom":subQ0})])],"isStart":true});}
            var Q10;
            {var subQ0=sQuery(id+"F0.wireOp",EDGE,"E12.0");var subQ1=sQuery(id+"F0.wireOp",EDGE,"E9.0");Q10=makeQuery(id+"F2.opFillet","BLEND_EDGE",EDGE,{"blendedFrom":[makeQuery(id+"F1.opExtrude","SWEPT_EDGE",EDGE,{"disambiguationData":[OSD([subQ1,subQ0]),TDD([makeQuery(id+"F0.imprint","INTERSECT",VERTEX,{"disambiguationData":[OD(0.0)],"derivedFrom":[subQ1,subQ0]})])]}),makeQuery(id+"F1.opExtrude","CAP_FACE",FACE,{"disambiguationData":[OSD([sQuery(id+"F0.wireOp",EDGE,"E0"),sQuery(id+"F0.wireOp",EDGE,"E1"),sQuery(id+"F0.wireOp",EDGE,"E3"),sQuery(id+"F0.wireOp",EDGE,"E6"),subQ1,sQuery(id+"F0.wireOp",EDGE,"E10.0"),sQuery(id+"F0.wireOp",EDGE,"E11.0"),subQ0,sQuery(id+"F0.wireOp",EDGE,"E13"),sQuery(id+"F0.wireOp",EDGE,"E14"),sQuery(id+"F0.wireOp",EDGE,"E15"),sQuery(id+"F0.wireOp",EDGE,"E16"),sQuery(id+"F0.wireOp",EDGE,"E17"),sQuery(id+"F0.wireOp",EDGE,"E19"),sQuery(id+"F0.wireOp",EDGE,"E20"),sQuery(id+"F0.wireOp",EDGE,"E22"),sQuery(id+"F0.wireOp",EDGE,"E24")])],"isStart":true})],"blendedInto":[makeQuery(id+"F1.opExtrude","CAP_FACE",FACE,{"disambiguationData":[OSD([sQuery(id+"F0.wireOp",EDGE,"E0"),sQuery(id+"F0.wireOp",EDGE,"E1"),sQuery(id+"F0.wireOp",EDGE,"E3"),sQuery(id+"F0.wireOp",EDGE,"E6"),subQ1,sQuery(id+"F0.wireOp",EDGE,"E10.0"),sQuery(id+"F0.wireOp",EDGE,"E11.0"),subQ0,sQuery(id+"F0.wireOp",EDGE,"E13"),sQuery(id+"F0.wireOp",EDGE,"E14"),sQuery(id+"F0.wireOp",EDGE,"E15"),sQuery(id+"F0.wireOp",EDGE,"E16"),sQuery(id+"F0.wireOp",EDGE,"E17"),sQuery(id+"F0.wireOp",EDGE,"E19"),sQuery(id+"F0.wireOp",EDGE,"E20"),sQuery(id+"F0.wireOp",EDGE,"E22"),sQuery(id+"F0.wireOp",EDGE,"E24")])],"isStart":true})]});}
            var Q11;
            {var subQ0=sQuery(id+"F0.wireOp",EDGE,"E12.0");Q11=makeQuery(id+"F1.opExtrude","CAP_EDGE",EDGE,{"disambiguationData":[OSD([subQ0]),TDD([makeQuery(id+"F0.imprint","IMPRINT",EDGE,{"disambiguationData":[TD([[makeQuery(id+"F0.imprint","INTERSECT",VERTEX,{"derivedFrom":[subQ0,sQuery(id+"F0.wireOp",EDGE,"E15")]}),1.0]])],"derivedFrom":subQ0})])],"isStart":true});}
            var Q12;
            {var subQ0=sQuery(id+"F0.wireOp",EDGE,"E12.0");var subQ1=sQuery(id+"F0.wireOp",EDGE,"E10.0");var subQ2=sQuery(id+"F0.wireOp",EDGE,"E3");var subQ3=sQuery(id+"F0.wireOp",EDGE,"E1");var subQ4=sQuery(id+"F0.wireOp",EDGE,"E11.0");var subQ5=sQuery(id+"F0.wireOp",EDGE,"E6");var subQ6=sQuery(id+"F0.wireOp",EDGE,"E9.0");var subQ7=sQuery(id+"F0.wireOp",EDGE,"E0");var subQ8=sQuery(id+"F0.wireOp",EDGE,"E15");Q12=makeQuery(id+"F8.opFillet","BLEND_EDGE",EDGE,{"blendedFrom":[makeQuery(id+"F1.opExtrude","SWEPT_EDGE",EDGE,{"disambiguationData":[OSD([subQ0,subQ8])]}),makeQuery(id+"F4.boolean.opBoolean","MERGE",FACE,{"derivedFrom":[makeQuery(id+"F1.opExtrude","CAP_FACE",FACE,{"disambiguationData":[OSD([subQ7,subQ3,subQ2,subQ5,subQ6,subQ1,subQ4,subQ0,sQuery(id+"F0.wireOp",EDGE,"E13"),sQuery(id+"F0.wireOp",EDGE,"E14"),subQ8,sQuery(id+"F0.wireOp",EDGE,"E16"),sQuery(id+"F0.wireOp",EDGE,"E17"),sQuery(id+"F0.wireOp",EDGE,"E19"),sQuery(id+"F0.wireOp",EDGE,"E20"),sQuery(id+"F0.wireOp",EDGE,"E22"),sQuery(id+"F0.wireOp",EDGE,"E24")])],"isStart":true}),makeQuery(id+"F4.opExtrude","CAP_FACE",FACE,{"disambiguationData":[OSD([subQ7,subQ3,subQ6,subQ0])],"isStart":true}),makeQuery(id+"F4.opExtrude","CAP_FACE",FACE,{"disambiguationData":[OSD([subQ3,subQ5,subQ4,subQ0])],"isStart":true}),makeQuery(id+"F4.opExtrude","CAP_FACE",FACE,{"disambiguationData":[OSD([subQ3,subQ2,subQ1,subQ0])],"isStart":true})]})],"blendedInto":[makeQuery(id+"F4.boolean.opBoolean","MERGE",FACE,{"derivedFrom":[makeQuery(id+"F1.opExtrude","CAP_FACE",FACE,{"disambiguationData":[OSD([subQ7,subQ3,subQ2,subQ5,subQ6,subQ1,subQ4,subQ0,sQuery(id+"F0.wireOp",EDGE,"E13"),sQuery(id+"F0.wireOp",EDGE,"E14"),subQ8,sQuery(id+"F0.wireOp",EDGE,"E16"),sQuery(id+"F0.wireOp",EDGE,"E17"),sQuery(id+"F0.wireOp",EDGE,"E19"),sQuery(id+"F0.wireOp",EDGE,"E20"),sQuery(id+"F0.wireOp",EDGE,"E22"),sQuery(id+"F0.wireOp",EDGE,"E24")])],"isStart":true}),makeQuery(id+"F4.opExtrude","CAP_FACE",FACE,{"disambiguationData":[OSD([subQ7,subQ3,subQ6,subQ0])],"isStart":true}),makeQuery(id+"F4.opExtrude","CAP_FACE",FACE,{"disambiguationData":[OSD([subQ3,subQ5,subQ4,subQ0])],"isStart":true}),makeQuery(id+"F4.opExtrude","CAP_FACE",FACE,{"disambiguationData":[OSD([subQ3,subQ2,subQ1,subQ0])],"isStart":true})]})]});}
            var Q13;
            Q13=makeQuery(id+"F1.opExtrude","CAP_EDGE",EDGE,{"disambiguationData":[OSD([sQuery(id+"F0.wireOp",EDGE,"E16")])],"isStart":true});
            var Q14;
            {var subQ0=sQuery(id+"F0.wireOp",EDGE,"E12.0");var subQ1=sQuery(id+"F0.wireOp",EDGE,"E10.0");var subQ2=sQuery(id+"F0.wireOp",EDGE,"E3");var subQ3=sQuery(id+"F0.wireOp",EDGE,"E1");var subQ4=sQuery(id+"F0.wireOp",EDGE,"E11.0");var subQ5=sQuery(id+"F0.wireOp",EDGE,"E6");var subQ6=sQuery(id+"F0.wireOp",EDGE,"E9.0");var subQ7=sQuery(id+"F0.wireOp",EDGE,"E0");var subQ8=sQuery(id+"F0.wireOp",EDGE,"E20");var subQ9=sQuery(id+"F0.wireOp",EDGE,"E16");Q14=makeQuery(id+"F7.opFillet","BLEND_EDGE",EDGE,{"blendedFrom":[makeQuery(id+"F1.opExtrude","SWEPT_EDGE",EDGE,{"disambiguationData":[OSD([subQ9,subQ8])]}),makeQuery(id+"F4.boolean.opBoolean","MERGE",FACE,{"derivedFrom":[makeQuery(id+"F1.opExtrude","CAP_FACE",FACE,{"disambiguationData":[OSD([subQ7,subQ3,subQ2,subQ5,subQ6,subQ1,subQ4,subQ0,sQuery(id+"F0.wireOp",EDGE,"E13"),sQuery(id+"F0.wireOp",EDGE,"E14"),sQuery(id+"F0.wireOp",EDGE,"E15"),subQ9,sQuery(id+"F0.wireOp",EDGE,"E17"),sQuery(id+"F0.wireOp",EDGE,"E19"),subQ8,sQuery(id+"F0.wireOp",EDGE,"E22"),sQuery(id+"F0.wireOp",EDGE,"E24")])],"isStart":true}),makeQuery(id+"F4.opExtrude","CAP_FACE",FACE,{"disambiguationData":[OSD([subQ7,subQ3,subQ6,subQ0])],"isStart":true}),makeQuery(id+"F4.opExtrude","CAP_FACE",FACE,{"disambiguationData":[OSD([subQ3,subQ5,subQ4,subQ0])],"isStart":true}),makeQuery(id+"F4.opExtrude","CAP_FACE",FACE,{"disambiguationData":[OSD([subQ3,subQ2,subQ1,subQ0])],"isStart":true})]})],"blendedInto":[makeQuery(id+"F4.boolean.opBoolean","MERGE",FACE,{"derivedFrom":[makeQuery(id+"F1.opExtrude","CAP_FACE",FACE,{"disambiguationData":[OSD([subQ7,subQ3,subQ2,subQ5,subQ6,subQ1,subQ4,subQ0,sQuery(id+"F0.wireOp",EDGE,"E13"),sQuery(id+"F0.wireOp",EDGE,"E14"),sQuery(id+"F0.wireOp",EDGE,"E15"),subQ9,sQuery(id+"F0.wireOp",EDGE,"E17"),sQuery(id+"F0.wireOp",EDGE,"E19"),subQ8,sQuery(id+"F0.wireOp",EDGE,"E22"),sQuery(id+"F0.wireOp",EDGE,"E24")])],"isStart":true}),makeQuery(id+"F4.opExtrude","CAP_FACE",FACE,{"disambiguationData":[OSD([subQ7,subQ3,subQ6,subQ0])],"isStart":true}),makeQuery(id+"F4.opExtrude","CAP_FACE",FACE,{"disambiguationData":[OSD([subQ3,subQ5,subQ4,subQ0])],"isStart":true}),makeQuery(id+"F4.opExtrude","CAP_FACE",FACE,{"disambiguationData":[OSD([subQ3,subQ2,subQ1,subQ0])],"isStart":true})]})]});}
            var Q15;
            {var subQ0=sQuery(id+"F0.wireOp",EDGE,"E11.0");Q15=makeQuery(id+"F1.opExtrude","CAP_EDGE",EDGE,{"disambiguationData":[OSD([subQ0]),TDD([makeQuery(id+"F0.imprint","IMPRINT",EDGE,{"disambiguationData":[TD([[makeQuery(id+"F0.imprint","INTERSECT",VERTEX,{"derivedFrom":[subQ0,sQuery(id+"F0.wireOp",EDGE,"E20")]}),-1.0]])],"derivedFrom":subQ0})])],"isStart":true});}
            var Q16;
            {var subQ0=sQuery(id+"F0.wireOp",EDGE,"E12.0");var subQ1=sQuery(id+"F0.wireOp",EDGE,"E10.0");var subQ2=sQuery(id+"F0.wireOp",EDGE,"E3");var subQ3=sQuery(id+"F0.wireOp",EDGE,"E1");var subQ4=sQuery(id+"F0.wireOp",EDGE,"E11.0");var subQ5=sQuery(id+"F0.wireOp",EDGE,"E6");var subQ6=sQuery(id+"F0.wireOp",EDGE,"E9.0");var subQ7=sQuery(id+"F0.wireOp",EDGE,"E0");var subQ8=sQuery(id+"F0.wireOp",EDGE,"E20");Q16=makeQuery(id+"F6.opFillet","BLEND_EDGE",EDGE,{"blendedFrom":[makeQuery(id+"F1.opExtrude","SWEPT_EDGE",EDGE,{"disambiguationData":[OSD([subQ4,subQ8])]}),makeQuery(id+"F4.boolean.opBoolean","MERGE",FACE,{"derivedFrom":[makeQuery(id+"F1.opExtrude","CAP_FACE",FACE,{"disambiguationData":[OSD([subQ7,subQ3,subQ2,subQ5,subQ6,subQ1,subQ4,subQ0,sQuery(id+"F0.wireOp",EDGE,"E13"),sQuery(id+"F0.wireOp",EDGE,"E14"),sQuery(id+"F0.wireOp",EDGE,"E15"),sQuery(id+"F0.wireOp",EDGE,"E16"),sQuery(id+"F0.wireOp",EDGE,"E17"),sQuery(id+"F0.wireOp",EDGE,"E19"),subQ8,sQuery(id+"F0.wireOp",EDGE,"E22"),sQuery(id+"F0.wireOp",EDGE,"E24")])],"isStart":true}),makeQuery(id+"F4.opExtrude","CAP_FACE",FACE,{"disambiguationData":[OSD([subQ7,subQ3,subQ6,subQ0])],"isStart":true}),makeQuery(id+"F4.opExtrude","CAP_FACE",FACE,{"disambiguationData":[OSD([subQ3,subQ5,subQ4,subQ0])],"isStart":true}),makeQuery(id+"F4.opExtrude","CAP_FACE",FACE,{"disambiguationData":[OSD([subQ3,subQ2,subQ1,subQ0])],"isStart":true})]})],"blendedInto":[makeQuery(id+"F4.boolean.opBoolean","MERGE",FACE,{"derivedFrom":[makeQuery(id+"F1.opExtrude","CAP_FACE",FACE,{"disambiguationData":[OSD([subQ7,subQ3,subQ2,subQ5,subQ6,subQ1,subQ4,subQ0,sQuery(id+"F0.wireOp",EDGE,"E13"),sQuery(id+"F0.wireOp",EDGE,"E14"),sQuery(id+"F0.wireOp",EDGE,"E15"),sQuery(id+"F0.wireOp",EDGE,"E16"),sQuery(id+"F0.wireOp",EDGE,"E17"),sQuery(id+"F0.wireOp",EDGE,"E19"),subQ8,sQuery(id+"F0.wireOp",EDGE,"E22"),sQuery(id+"F0.wireOp",EDGE,"E24")])],"isStart":true}),makeQuery(id+"F4.opExtrude","CAP_FACE",FACE,{"disambiguationData":[OSD([subQ7,subQ3,subQ6,subQ0])],"isStart":true}),makeQuery(id+"F4.opExtrude","CAP_FACE",FACE,{"disambiguationData":[OSD([subQ3,subQ5,subQ4,subQ0])],"isStart":true}),makeQuery(id+"F4.opExtrude","CAP_FACE",FACE,{"disambiguationData":[OSD([subQ3,subQ2,subQ1,subQ0])],"isStart":true})]})]});}
            var Q17;
            Q17=makeQuery(id+"F1.opExtrude","CAP_EDGE",EDGE,{"disambiguationData":[OSD([sQuery(id+"F0.wireOp",EDGE,"E20")])],"isStart":true});
            var Q18;
            Q18=makeQuery(id+"F1.opExtrude","CAP_EDGE",EDGE,{"disambiguationData":[OSD([sQuery(id+"F0.wireOp",EDGE,"E13")])],"isStart":true});
            fillet(context, id + "F10", {"entities" : qUnion([Q0, Q1, Q2, Q3, Q4, Q5, Q6, Q7, Q8, Q9, Q10, Q11, Q12, Q13, Q14, Q15, Q16, Q17, Q18]), "radius" : .5 * mm, "tangentPropagation" : true, "allowEdgeOverflow" : false});
        }
    });
